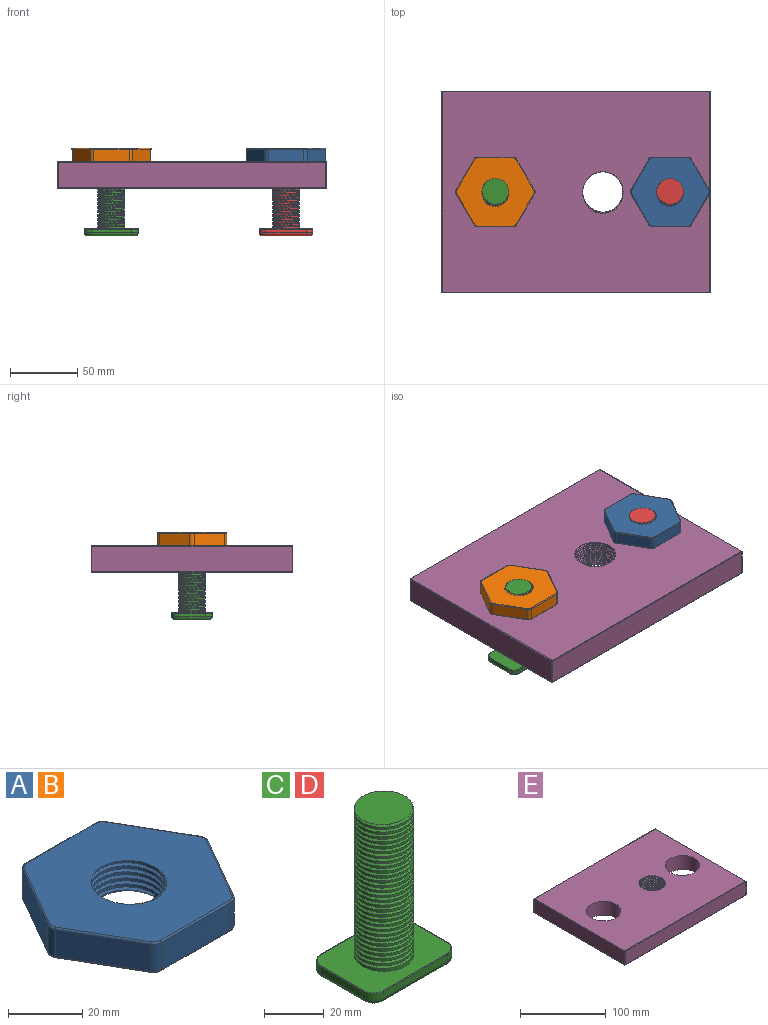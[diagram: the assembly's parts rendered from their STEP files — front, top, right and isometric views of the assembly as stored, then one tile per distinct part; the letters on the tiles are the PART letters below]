
ASSEMBLY  parts=5 mates=6
PART A: 42 faces, bbox 59.9x52.8x11 mm
  f0: plane 22.98x13.27mm, normal (0.87,0.5,0), area 238.8mm2, adj f1,f12,f21,f38
  f1: cylinder r=3mm len=9mm, axis (0,0,-1), area 28.3mm2, adj f0,f2,f19,f37
  f2: plane 26.54x9mm, normal (0,1,0), area 238.8mm2, adj f1,f3,f17,f35
  f3: cylinder r=3mm len=9mm, axis (0,0,-1), area 28.3mm2, adj f2,f4,f15,f33
  f4: plane 22.98x13.27mm, normal (-0.87,0.5,0), area 238.8mm2, adj f3,f5,f16,f31
  f5: cylinder r=3mm len=9mm, axis (0,0,-1), area 28.3mm2, adj f4,f6,f18,f29
  f6: plane 22.98x13.27mm, normal (-0.87,-0.5,0), area 238.8mm2, adj f5,f7,f20,f27
  f7: cylinder r=3mm len=9mm, axis (0,0,-1), area 28.3mm2, adj f6,f8,f22,f28
  f8: plane 26.54x9mm, normal (0,-1,0), area 238.8mm2, adj f7,f9,f24,f30
  f9: cylinder r=3mm len=9mm, axis (0,0,-1), area 28.3mm2, adj f8,f10,f26,f32
  f10: plane 22.98x13.27mm, normal (0.87,-0.5,0), area 238.8mm2, adj f9,f12,f25,f34
  f11: cylinder r=10mm len=20mm, axis (0,0,-1), area 332.6mm2, adj f13,f14,f39,f40,f41
  f12: cylinder r=3mm len=9mm, axis (0,0,-1), area 28.3mm2, adj f0,f10,f23,f36
  f13: plane 58.39x51.28mm, normal (0,0,1), area 1919mm2, adj f11,f15,f16,f17,f18,f19,f20,f21
  f14: plane 58.07x50.96mm, normal (0,0,-1), area 1933mm2, adj f11,f27,f28,f29,f30,f31,f32,f33
  f15: torus R=2.5mm, axis (0,0,1), area 2.3mm2, adj f3,f13,f16,f17
  f16: cylinder r=0.5mm len=23.23mm, axis (0.5,0.87,0), area 20.8mm2, adj f4,f13,f15,f18
  f17: cylinder r=0.5mm len=26.54mm, axis (1,0,0), area 20.8mm2, adj f2,f13,f15,f19
  f18: torus R=2.5mm, axis (0,0,1), area 2.3mm2, adj f5,f13,f16,f20
  f19: torus R=2.5mm, axis (0,0,1), area 2.3mm2, adj f1,f13,f17,f21
  f20: cylinder r=0.5mm len=23.23mm, axis (-0.5,0.87,0), area 20.8mm2, adj f6,f13,f18,f22
  f21: cylinder r=0.5mm len=23.23mm, axis (0.5,-0.87,0), area 20.8mm2, adj f0,f13,f19,f23
  f22: torus R=2.5mm, axis (0,0,1), area 2.3mm2, adj f7,f13,f20,f24
  f23: torus R=2.5mm, axis (0,0,1), area 2.3mm2, adj f12,f13,f21,f25
  f24: cylinder r=0.5mm len=26.54mm, axis (-1,0,0), area 20.8mm2, adj f8,f13,f22,f26
  f25: cylinder r=0.5mm len=23.23mm, axis (-0.5,-0.87,0), area 20.8mm2, adj f10,f13,f23,f26
  f26: torus R=2.5mm, axis (0,0,1), area 2.3mm2, adj f9,f13,f24,f25
  f27: cylinder r=0.5mm len=23.23mm, axis (0.5,-0.87,0), area 20.8mm2, adj f6,f14,f28,f29
  f28: torus R=2.5mm, axis (0,0,1), area 2.3mm2, adj f7,f14,f27,f30
  f29: torus R=2.5mm, axis (0,0,1), area 2.3mm2, adj f5,f14,f27,f31
  f30: cylinder r=0.5mm len=26.54mm, axis (1,0,0), area 20.8mm2, adj f8,f14,f28,f32
  f31: cylinder r=0.5mm len=23.23mm, axis (-0.5,-0.87,0), area 20.8mm2, adj f4,f14,f29,f33
  f32: torus R=2.5mm, axis (0,0,1), area 2.3mm2, adj f9,f14,f30,f34
  f33: torus R=2.5mm, axis (0,0,1), area 2.3mm2, adj f3,f14,f31,f35
  f34: cylinder r=0.5mm len=23.23mm, axis (0.5,0.87,0), area 20.8mm2, adj f10,f14,f32,f36
  f35: cylinder r=0.5mm len=26.54mm, axis (-1,0,0), area 20.8mm2, adj f2,f14,f33,f37
  f36: torus R=2.5mm, axis (0,0,1), area 2.3mm2, adj f12,f14,f34,f38
  f37: torus R=2.5mm, axis (0,0,1), area 2.3mm2, adj f1,f14,f35,f38
  f38: cylinder r=0.5mm len=23.23mm, axis (-0.5,0.87,0), area 20.8mm2, adj f0,f14,f36,f37
  f39: plane 1x0.87mm, normal (0,1,0), area 0.4mm2, adj f11,f40,f41
  f40: bspline ~25.09x21.73mm, area 303.8mm2, adj f11,f13,f39,f41
  f41: bspline ~25.09x21.73mm, area 319.5mm2, adj f11,f13,f39,f40
PART B: same geometry as A
PART C: 31 faces, bbox 41.3x31.3x66.1 mm
  f0: cylinder r=10mm len=60mm, axis (0,0,-1), area 1467.7mm2, adj f1,f11,f28,f29,f30
  f1: plane 20.44x19.6mm, normal (0,0,1), area 301mm2, adj f0,f29,f30
  f2: plane 20x2.8mm, normal (1,0,0), area 56mm2, adj f3,f9,f15,f23
  f3: cylinder r=5mm len=5mm, axis (0,0,1), area 22mm2, adj f2,f4,f13,f21
  f4: plane 30x2.8mm, normal (0,-1,0), area 84mm2, adj f3,f5,f12,f20
  f5: cylinder r=5mm len=5mm, axis (0,0,1), area 22mm2, adj f4,f6,f14,f22
  f6: plane 20x2.8mm, normal (-1,0,0), area 56mm2, adj f5,f7,f16,f24
  f7: cylinder r=5mm len=5mm, axis (0,0,1), area 22mm2, adj f6,f8,f18,f26
  f8: plane 30x2.8mm, normal (0,1,0), area 84mm2, adj f7,f9,f19,f27
  f9: cylinder r=5mm len=5mm, axis (0,0,1), area 22mm2, adj f2,f8,f17,f25
  f10: plane 36x26mm, normal (0,0,-1), area 928.3mm2, adj f12,f13,f14,f15,f16,f17,f18,f19
  f11: plane 39.6x29.6mm, normal (0,0,1), area 838.2mm2, adj f0,f20,f21,f22,f23,f24,f25,f26
  f12: cylinder r=2mm len=30mm, axis (1,0,0), area 94.2mm2, adj f4,f10,f13,f14
  f13: torus R=3mm, axis (0,0,-1), area 21.1mm2, adj f3,f10,f12,f15
  f14: torus R=3mm, axis (0,0,-1), area 21.1mm2, adj f5,f10,f12,f16
  f15: cylinder r=2mm len=20mm, axis (0,1,0), area 62.8mm2, adj f2,f10,f13,f17
  f16: cylinder r=2mm len=20mm, axis (0,-1,0), area 62.8mm2, adj f6,f10,f14,f18
  f17: torus R=3mm, axis (0,0,-1), area 21.1mm2, adj f9,f10,f15,f19
  f18: torus R=3mm, axis (0,0,-1), area 21.1mm2, adj f7,f10,f16,f19
  f19: cylinder r=2mm len=30mm, axis (-1,0,0), area 94.2mm2, adj f8,f10,f17,f18
  f20: cylinder r=0.2mm len=30mm, axis (-1,0,0), area 9.4mm2, adj f4,f11,f21,f22
  f21: torus R=4.8mm, axis (0,0,-1), area 2.4mm2, adj f3,f11,f20,f23
  f22: torus R=4.8mm, axis (0,0,-1), area 2.4mm2, adj f5,f11,f20,f24
  f23: cylinder r=0.2mm len=20mm, axis (0,-1,0), area 6.3mm2, adj f2,f11,f21,f25
  f24: cylinder r=0.2mm len=20mm, axis (0,1,0), area 6.3mm2, adj f6,f11,f22,f26
  f25: torus R=4.8mm, axis (0,0,-1), area 2.4mm2, adj f9,f11,f23,f27
  f26: torus R=4.8mm, axis (0,0,-1), area 2.4mm2, adj f7,f11,f24,f27
  f27: cylinder r=0.2mm len=30mm, axis (1,0,0), area 9.4mm2, adj f8,f11,f25,f26
  f28: plane 1x0.87mm, normal (0,1,0), area 0.4mm2, adj f0,f29,f30
  f29: bspline ~60.17x23.09mm, area 1785.9mm2, adj f0,f1,f28,f30
  f30: bspline ~60.5x23.09mm, area 1792.2mm2, adj f0,f1,f28,f29
PART D: same geometry as C
PART E: 32 faces, bbox 200.4x150.4x21 mm
  f0: cylinder r=15mm len=30mm, axis (0,0,1), area 863.5mm2, adj f5,f6,f29,f30,f31
  f1: plane 199x19mm, normal (0,1,0), area 3781mm2, adj f17,f22,f25,f28
  f2: plane 149x19mm, normal (-1,0,0), area 2831mm2, adj f14,f23,f24,f28
  f3: plane 199x19mm, normal (0,-1,0), area 3781mm2, adj f9,f13,f14,f15
  f4: plane 149x19mm, normal (1,0,0), area 2831mm2, adj f9,f12,f16,f17
  f5: plane 199.36x149.36mm, normal (0,0,1), area 26410.1mm2, adj f0,f7,f8,f12,f13,f22,f23,f30
  f6: plane 199x149mm, normal (0,0,-1), area 26430.9mm2, adj f0,f7,f8,f15,f16,f24,f25
  f7: cylinder r=20mm len=40mm, axis (0,0,1), area 2513.3mm2, adj f5,f6
  f8: cylinder r=20mm len=40mm, axis (0,0,1), area 2513.3mm2, adj f5,f6
  f9: cylinder r=0.5mm len=19mm, axis (0,0,1), area 14.9mm2, adj f3,f4,f10,f11
  f10: sphere r=0.5mm, area 0.4mm2, adj f9,f12,f13
  f11: sphere r=0.5mm, area 0.4mm2, adj f9,f15,f16
  f12: cylinder r=0.5mm len=149mm, axis (0,-1,0), area 117mm2, adj f4,f5,f10,f18
  f13: cylinder r=0.5mm len=199mm, axis (-1,0,0), area 156.3mm2, adj f3,f5,f10,f19
  f14: cylinder r=0.5mm len=19mm, axis (0,0,-1), area 14.9mm2, adj f2,f3,f19,f20
  f15: cylinder r=0.5mm len=199mm, axis (1,0,0), area 156.3mm2, adj f3,f6,f11,f20
  f16: cylinder r=0.5mm len=149mm, axis (0,1,0), area 117mm2, adj f4,f6,f11,f21
  f17: cylinder r=0.5mm len=19mm, axis (0,0,-1), area 14.9mm2, adj f1,f4,f18,f21
  f18: sphere r=0.5mm, area 0.2mm2, adj f12,f17,f22
  f19: sphere r=0.5mm, area 0.4mm2, adj f13,f14,f23
  f20: sphere r=0.5mm, area 0.4mm2, adj f14,f15,f24
  f21: sphere r=0.5mm, area 0.3mm2, adj f16,f17,f25
  f22: cylinder r=0.5mm len=199mm, axis (1,0,0), area 156.3mm2, adj f1,f5,f18,f26
  f23: cylinder r=0.5mm len=149mm, axis (0,1,0), area 117mm2, adj f2,f5,f19,f26
  f24: cylinder r=0.5mm len=149mm, axis (0,-1,0), area 117mm2, adj f2,f6,f20,f27
  f25: cylinder r=0.5mm len=199mm, axis (-1,0,0), area 156.3mm2, adj f1,f6,f21,f27
  f26: sphere r=0.5mm, area 0.5mm2, adj f22,f23,f28
  f27: sphere r=0.5mm, area 0.5mm2, adj f24,f25,f28
  f28: cylinder r=0.5mm len=19mm, axis (0,0,1), area 14.9mm2, adj f1,f2,f26,f27
  f29: plane 1x0.87mm, normal (0,1,0), area 0.4mm2, adj f0,f30,f31
  f30: bspline ~36.64x31.73mm, area 932.7mm2, adj f0,f5,f29,f31
  f31: bspline ~36.64x31.73mm, area 958.2mm2, adj f0,f5,f29,f30
PLACE A t=(93.09,105.84,59.47)mm
PLACE B t=(-36.91,105.84,59.47)mm
PLACE C t=(-36.91,105.84,34.47)mm
PLACE D t=(93.09,105.84,34.47)mm
PLACE E t=(23.09,105.84,34.47)mm
MATE cylindrical D.f0 <-> A.f11  axis (0,0,1) through (93.09,105.84,64.47)mm
MATE cylindrical C.f0 <-> B.f11  axis (0,0,1) through (-36.91,105.84,64.47)mm
MATE planar A.f11 <-> E.f8  axis (0,0,-1) through (93.09,105.84,54.47)mm
MATE planar D.f0 <-> A.f11  axis (0,0,1) through (93.09,105.84,64.47)mm
MATE planar C.f0 <-> B.f11  axis (0,0,1) through (-36.91,105.84,64.47)mm
MATE planar B.f11 <-> E.f7  axis (0,0,-1) through (-36.91,105.84,54.47)mm
